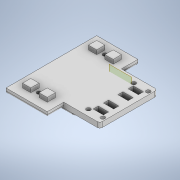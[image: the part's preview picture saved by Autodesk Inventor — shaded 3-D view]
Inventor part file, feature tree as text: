
AUTODESK INVENTOR PART (.ipt)
format: ipt  version: 2022 (Build 260153000, 153)  size: 727,552 bytes
history: native  units: in
note: dims shown in document units (in); Inventor stores cm internally (conversion verified against a paired STEP export)
features: extrude x11, sketch x11, fillet x5, mirror x3, plane x1
ambient origin geometry x8: Origin, YZ Plane, XZ Plane, XY Plane, X Axis, Y Axis, Z Axis, Center Point
bodies: Solid1 (feature_tree)
feature tree (31):
  extrude  "Extrusion1"  Depth=3.4646in
  extrude  "Extrusion2"  Depth=0.1969in
  extrude  "Extrusion3"  Depth=0.315in
  extrude  "Extrusion4"  Depth=0.1969in TaperAngle=0.0deg
  fillet  "Fillet1"  Radius=0.1575in
  fillet  "Fillet2"  Radius=0.1969in
  extrude  "Extrusion5"  Depth=0.1969in
  plane  "Work Plane1"
  mirror  "Mirror1"
  fillet  "Fillet4"  Radius=0.0984in
  extrude  "Extrusion8"  Depth=0.0984in
  extrude  "Extrusion9"  Depth=0.098in
  extrude  "Extrusion10"  TaperAngle=90.0deg  [1 undecoded]
  mirror  "Mirror2"
  extrude  "Extrusion11"  Depth=1.1811in
  extrude  "Extrusion12"  Depth=1.1811in
  extrude  "Extrusion13"  Depth=0.0984in
  fillet  "Fillet5"  Radius=0.6528in
  mirror  "Mirror3"
  fillet  "Fillet6"  Radius=0.6528in
  sketch  "Sketch1"  dims[d0=1.5748in d1=3.4646in]
  sketch  "Sketch2"  dims[d2=0.1969in d3=0.0in d4=0.315in]
  sketch  "Sketch3"  dims[d5=0.315in d6=0.315in]
  sketch  "Sketch4"  dims[d7=0.315in d8=0.1575in d9=0.0in d10=0.1575in d11=0.1969in d12=0.0in]
  sketch  "Sketch5"  dims[d13=0.1969in d14=0.1969in d15=0.0984in d16=0.0in]
  sketch  "Sketch8"  dims[d17=0.0984in d18=0.0984in]
  sketch  "Sketch9"  dims[d19=0.2756in d20=0.0in d33=0.098in]
  sketch  "Sketch10"  dims[d34=0.7874in d35=90.0deg]
  sketch  "Sketch11"  dims[d36=0.4134in d37=1.1811in]
  sketch  "Sketch12"  dims[d38=1.1811in d39=0.1083in]
  sketch  "Sketch13"  dims[d40=0.1083in d43=0.8661in d44=0.4547in d45=1.2992in d46=1.2992in d47=0.1191in d48=0.1191in d49=0.9843in d50=0.6528in d51=0.6528in d52=1.378in d55=90.0deg d56=1.378in d57=3.1496in d58=2.3622in d59=2.3622in d60=0.189in d61=2.1654in d62=0.1811in d63=1.9685in d64=0.1693in d65=1.7717in d66=0.1575in d67=1.7717in d68=0.1476in d69=1.5748in d70=0.1398in d71=1.378in d72=0.135in d73=1.1811in d74=0.1329in d75=0.9843in d76=0.1331in d77=0.7874in d87=0.3937in d88=0.0515in d90=0.0984in d91=45.0deg d94=0.1181in d95=0.1476in d96=0.2953in d97=0.2362in d98=180.0deg d99=180.0deg d100=0.1969in d101=0.1969in d102=0.3937in d103=0.0412in d104=2.3622in d105=0.3937in d106=0.0412in d107=2.3622in d108=0.0787in d109=45.0deg d110=0.0413in d111=0.0787in d112=45.0deg d113=0.0413in d114=0.2756in d115=0.3937in d116=0.0in d117=0.3937in d118=0.0in d119=0.3543in d120=0.0412in d121=2.3622in d122=0.3543in d123=0.0412in d124=2.3622in d125=0.0591in d126=45.0deg d127=0.0311in d128=0.0591in d129=45.0deg d130=0.0311in d131=0.2756in d132=0.1181in d133=0.0in d134=0.7874in d135=90.0deg d136=0.4134in d137=1.1811in d138=1.1811in d139=0.1083in d140=0.1083in d141=0.8661in d142=0.4547in d143=1.2992in d144=1.2992in d145=0.9843in d146=0.6528in d147=0.6528in d148=90.0deg d149=3.1496in d150=2.3622in d151=2.3622in d152=0.189in d153=2.1654in d154=0.1811in d155=1.9685in d156=0.1693in d157=1.7717in d158=0.1575in d159=1.7717in d160=0.1476in d161=1.5748in d162=0.1398in d163=1.378in d164=0.135in d165=1.1811in d166=0.1329in d167=0.9843in d168=0.1331in d169=0.7874in d170=0.3937in d171=0.0515in d172=0.0984in d173=45.0deg d174=0.1181in d175=0.1476in d176=0.2953in d177=0.2362in d178=180.0deg d179=180.0deg d180=0.1969in d181=0.1969in d182=0.3937in d183=0.0412in d184=2.3622in d185=0.3937in d186=0.0412in d187=2.3622in d188=0.0787in d189=45.0deg d190=0.0413in d191=0.0787in d192=45.0deg d193=0.0413in d194=0.2756in d195=0.3937in d196=0.0in d197=0.3937in d198=0.0in d199=0.3543in d200=0.0412in d201=2.3622in d202=0.3543in d203=0.0412in d204=2.3622in d205=0.0591in d206=45.0deg d207=0.0311in d208=0.0591in d209=45.0deg d210=0.0311in d211=0.2756in d212=0.0787in d213=0.0in d214=0.7874in d215=90.0deg d216=0.4134in d217=1.1811in d218=1.1811in d219=0.1083in d220=0.1083in d221=0.8661in d222=0.4547in d223=1.2992in d224=1.2992in d225=0.9843in d226=0.6528in d227=0.6528in d228=90.0deg d229=3.1496in d230=2.3622in d231=2.3622in d232=0.189in d233=2.1654in d234=0.1811in d235=1.9685in d236=0.1693in d237=1.7717in d238=0.1575in d239=1.7717in d240=0.1476in d241=1.5748in d242=0.1398in d243=1.378in d244=0.135in d245=1.1811in d246=0.1329in d247=0.9843in d248=0.1331in d249=0.7874in d250=0.3937in d251=0.0515in d252=0.0984in d253=45.0deg d254=0.1181in d255=0.1476in d256=0.2953in d257=0.2362in d258=180.0deg d259=180.0deg d260=0.1969in d261=0.1969in d262=0.3937in d263=0.0412in d264=2.3622in d265=0.3937in d266=0.0412in d267=2.3622in d268=0.0787in d269=45.0deg d270=0.0413in d271=0.0787in d272=45.0deg d273=0.0413in d274=0.2756in d275=0.3937in d276=0.0in d277=0.3937in d278=0.0in d279=0.3543in d280=0.0412in d281=2.3622in d282=0.3543in d283=0.0412in d284=2.3622in d285=0.0591in d286=45.0deg d287=0.0311in d288=0.0591in d289=45.0deg d290=0.0311in d291=0.2756in d292=0.0591in d293=0.0in d294=1.1024in d295=0.0in d296=0.3937in d297=0.1969in d298=0.3937in d299=0.1969in d300=0.1575in d301=0.1575in d302=0.2362in d303=0.2362in d304=0.3346in d305=0.7283in d306=0.3937in d307=0.0in d308=0.9449in d309=0.0in d310=0.0984in d311=0.0984in]
note: 1 required parameter value undecoded (feature->parameter linkage not recoverable at this tier; creation-order binding heuristic only, values carry confidence <= 0.55)
